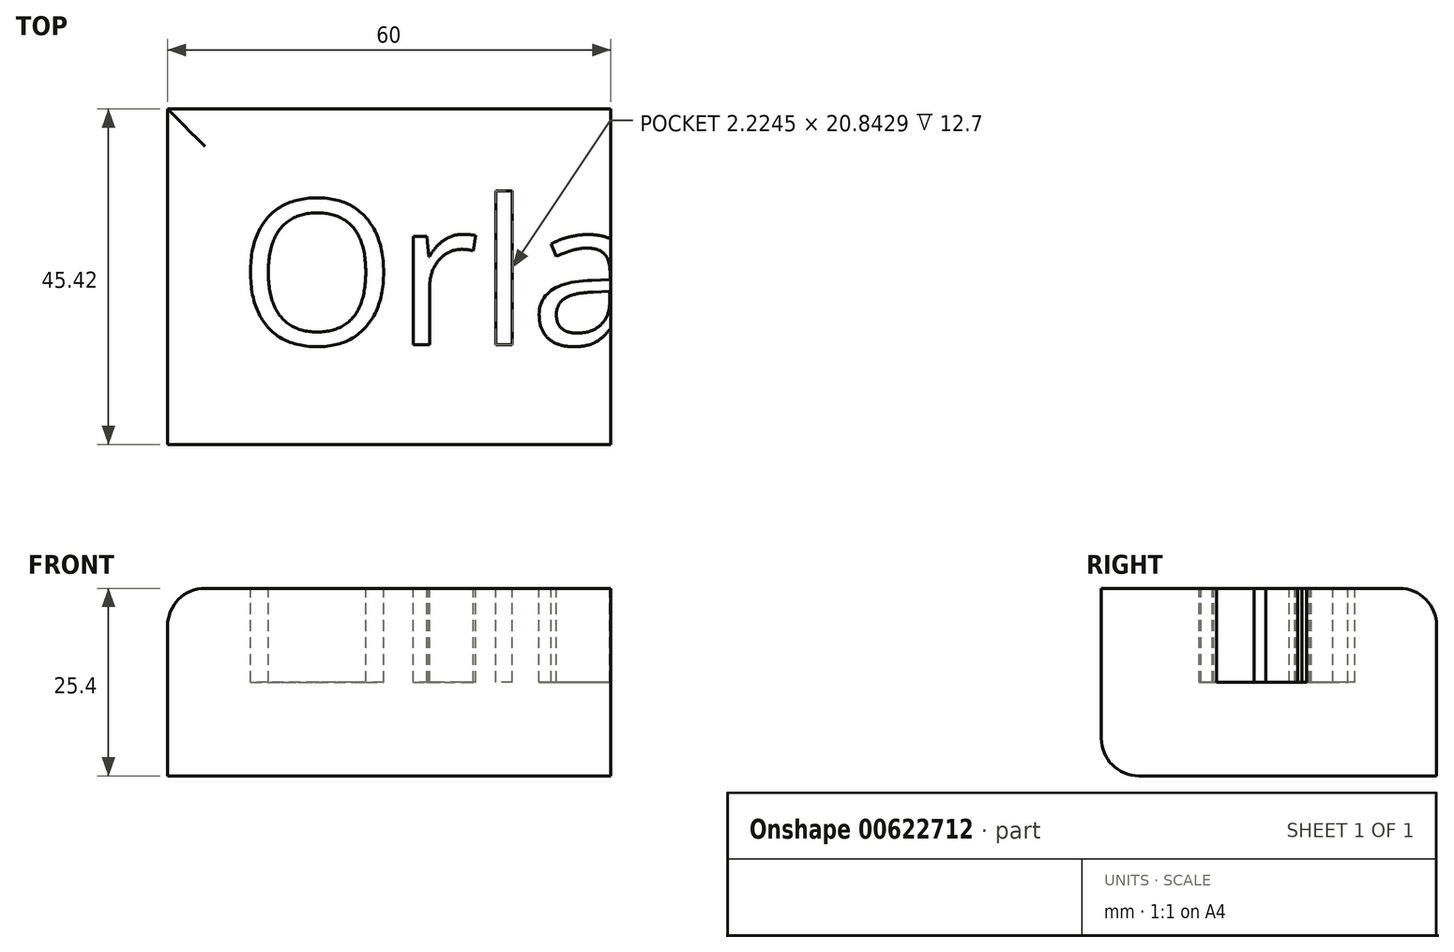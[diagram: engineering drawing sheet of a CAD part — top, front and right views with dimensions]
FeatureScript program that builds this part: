
annotation { "Feature Type Name" : "Feature", "Feature Type Description" : "" }
export const myFeature = defineFeature(function(context is Context, id is Id, definition is map)
    precondition{}
    {
        {
            var Q0;
            Q0=qCreatedBy(makeId("Top.planeOp"),FACE);
            var sketch = newSketch(context, id + "F0", { "sketchPlane" : qUnion([Q0])});
            skLineSegment(sketch, "E0.bottom", {"start": v(-14.85, 22.07) * mm, "end": v(-74.85, 22.07) * mm});
            skLineSegment(sketch, "E0.top", {"start": v(-14.85, -23.35) * mm, "end": v(-74.85, -23.35) * mm});
            skLineSegment(sketch, "E0.left", {"start": v(-14.85, 22.07) * mm, "end": v(-14.85, -23.35) * mm});
            skLineSegment(sketch, "E0.right", {"start": v(-74.85, 22.07) * mm, "end": v(-74.85, -23.35) * mm});
            skSolve(sketch);
        }
        {
            var Q0;
            Q0 = qSketchRegion(id + "F0", true);
            extrude(context, id + "F1", {"entities" : qUnion([Q0]), "depth" : 25.4 * mm, "offsetDistance" : 25.4 * mm});
        }
        {
            var Q0;
            Q0=makeQuery(id+"F1.opExtrude","CAP_FACE",FACE,{"disambiguationData":[OSD([sQuery(id+"F0.wireOp",EDGE,"E0.bottom"),sQuery(id+"F0.wireOp",EDGE,"E0.top"),sQuery(id+"F0.wireOp",EDGE,"E0.left"),sQuery(id+"F0.wireOp",EDGE,"E0.right")])],"isStart":false});
            var sketch = newSketch(context, id + "F2", { "sketchPlane" : qUnion([Q0])});
            skSolve(sketch);
        }
        {
            var Q0;
            Q0=makeQuery(id+"F2.imprint","IMPRINT",FACE,{"disambiguationData":[TD([[makeQuery(id+"F2.imprint","IMPRINT",EDGE,{"derivedFrom":makeQuery(id+"F1.opExtrude","CAP_EDGE",EDGE,{"disambiguationData":[OSD([sQuery(id+"F0.wireOp",EDGE,"E0.bottom")])],"isStart":false})}),1.0]])]});
            var sketch = newSketch(context, id + "F3", { "sketchPlane" : qUnion([Q0])});
            skText(sketch, "E1", { "text": "Orla", "fontName": "OpenSans-Regular.ttf"});
            const initialGuessF3  = {"E1": [-0.06529, -0.00985, 1, 0, 0.01975]};
            skSetInitialGuess(sketch, initialGuessF3);
            skSolve(sketch);
        }
        {
            var Q0;
            Q0 = qSketchRegion(id + "F3", true);
            extrude(context, id + "F4", {"entities" : qUnion([Q0]), "operationType" : NewBodyOperationType.REMOVE, "oppositeDirection" : true, "depth" : 12.7 * mm, "offsetDistance" : 25.4 * mm});
        }
        {
            var Q0;
            Q0=makeQuery(id+"F1.opExtrude","CAP_EDGE",EDGE,{"disambiguationData":[OSD([sQuery(id+"F0.wireOp",EDGE,"E0.bottom")])],"isStart":false});
            var Q1;
            Q1=makeQuery(id+"F1.opExtrude","CAP_EDGE",EDGE,{"disambiguationData":[OSD([sQuery(id+"F0.wireOp",EDGE,"E0.right")])],"isStart":false});
            var Q2;
            Q2=makeQuery(id+"F1.opExtrude","CAP_EDGE",EDGE,{"disambiguationData":[OSD([sQuery(id+"F0.wireOp",EDGE,"E0.top")])],"isStart":true});
            fillet(context, id + "F5", {"entities" : qUnion([Q0, Q1, Q2]), "radius" : 5.08 * mm, "tangentPropagation" : true, "allowEdgeOverflow" : false});
        }
    });
